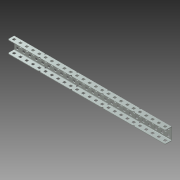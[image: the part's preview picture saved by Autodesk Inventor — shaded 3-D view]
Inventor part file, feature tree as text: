
AUTODESK INVENTOR PART (.ipt)
format: ipt  version: 2013 (Build 170138000, 138)  size: 2,703,360 bytes
history: native  units: mm (DEFAULTED — no unit token found)
features: other x124, extrude x124, pattern_linear x3, sketch x2, imported_body x1, plane x1, mirror x1
ambient origin geometry x8: Origin, YZ Plane, XZ Plane, XY Plane, X Axis, Y Axis, Z Axis, Center Point
bodies: Solid1 (feature_tree)
feature tree (256):
  imported_body  "Base1"
  sketch  "Sketch1"  dims[d1=1.1684mm]
  pattern_linear  "Rectangular Pattern1"  Spacing1=1.1684mm  [1 undecoded]
  pattern_linear  "Rectangular Pattern2"  Spacing1=0.0mm  [1 undecoded]
  pattern_linear  "Rectangular Pattern3"  Count1=25  [1 undecoded]
  plane  "Work Plane1"
  mirror  "Mirror1"
  other  "Srf1"
  other  "Srf2"
  other  "Srf3"
  other  "Srf4"
  other  "Srf5"
  other  "Srf6"
  other  "Srf7"
  other  "Srf8"
  other  "Srf9"
  other  "Srf10"
  other  "Srf11"
  other  "Srf12"
  other  "Srf13"
  other  "Srf14"
  other  "Srf15"
  other  "Srf16"
  other  "Srf17"
  other  "Srf18"
  other  "Srf19"
  other  "Srf20"
  other  "Srf21"
  other  "Srf22"
  other  "Srf23"
  other  "Srf24"
  other  "Srf25"
  other  "Srf26"
  other  "Srf27"
  other  "Srf28"
  other  "Srf29"
  other  "Srf30"
  other  "Srf31"
  other  "Srf32"
  other  "Srf33"
  other  "Srf34"
  other  "Srf35"
  other  "Srf36"
  other  "Srf37"
  other  "Srf38"
  other  "Srf39"
  other  "Srf40"
  other  "Srf41"
  other  "Srf42"
  other  "Srf43"
  other  "Srf44"
  other  "Srf45"
  other  "Srf46"
  other  "Srf47"
  other  "Srf48"
  other  "Srf49"
  other  "Srf50"
  other  "Srf51"
  other  "Srf52"
  other  "Srf53"
  other  "Srf54"
  other  "Srf55"
  other  "Srf56"
  other  "Srf57"
  other  "Srf58"
  other  "Srf59"
  other  "Srf60"
  other  "Srf61"
  other  "Srf62"
  other  "Srf63"
  other  "Srf64"
  other  "Srf65"
  other  "Srf66"
  other  "Srf67"
  other  "Srf68"
  other  "Srf69"
  other  "Srf70"
  other  "Srf71"
  other  "Srf72"
  other  "Srf73"
  other  "Srf74"
  sketch  "Sketch2"  dims[d2=0.0mm d3=1.1684mm d4=0.0mm d5=250.0mm d7=12.7mm d8=20.0mm d10=12.7mm d11=240.0mm d13=12.7mm d14=1.1684mm d15=0.0mm d16=250.0mm d18=12.7mm d19=0.0mm d20=0.0mm d21=0.0mm d22=0.0mm d23=0.0mm d24=0.0mm d25=0.0mm d26=0.0mm d27=0.0mm d28=0.0mm d29=0.0mm d30=0.0mm d31=0.0mm d32=0.0mm d33=0.0mm d34=0.0mm d35=0.0mm d36=0.0mm d37=0.0mm d38=0.0mm d39=0.0mm d40=0.0mm d41=0.0mm d42=0.0mm d43=0.0mm d44=0.0mm d45=0.0mm d46=0.0mm d47=0.0mm d48=0.0mm d49=0.0mm d50=0.0mm d51=0.0mm d52=0.0mm d53=0.0mm d54=0.0mm d55=0.0mm d56=0.0mm d57=0.0mm d58=0.0mm d59=0.0mm d60=0.0mm d61=0.0mm d62=0.0mm d63=0.0mm d64=0.0mm d65=0.0mm d66=0.0mm d67=0.0mm d68=0.0mm d69=0.0mm d70=0.0mm d71=0.0mm d72=0.0mm d73=0.0mm d74=0.0mm d75=0.0mm d76=0.0mm d77=0.0mm d78=0.0mm d79=0.0mm d80=0.0mm d81=0.0mm d82=0.0mm d83=0.0mm d84=0.0mm d85=0.0mm d86=0.0mm d87=0.0mm d88=0.0mm d89=0.0mm d90=0.0mm d91=0.0mm d92=0.0mm d93=0.0mm d94=0.0mm d95=0.0mm d96=0.0mm d97=0.0mm d98=0.0mm d99=0.0mm d100=0.0mm d101=0.0mm d102=0.0mm d103=0.0mm d104=0.0mm d105=0.0mm d106=0.0mm d107=0.0mm d108=0.0mm d109=0.0mm d110=0.0mm d111=0.0mm d112=0.0mm d113=0.0mm d114=0.0mm d115=0.0mm d116=0.0mm d117=0.0mm d118=0.0mm d119=0.0mm d120=0.0mm d121=0.0mm d122=0.0mm d123=0.0mm d124=0.0mm d125=0.0mm d126=0.0mm d127=0.0mm d128=0.0mm d129=0.0mm d130=0.0mm d131=0.0mm d132=0.0mm d133=0.0mm d134=0.0mm d135=0.0mm d136=0.0mm d137=0.0mm d138=0.0mm d139=0.0mm d140=0.0mm d141=0.0mm d142=0.0mm d143=0.0mm d144=0.0mm d145=0.0mm d146=0.0mm d147=0.0mm d148=0.0mm d149=0.0mm d150=0.0mm d151=0.0mm d152=0.0mm d153=0.0mm d154=0.0mm d155=0.0mm d156=0.0mm d157=0.0mm d158=0.0mm d159=0.0mm d160=0.0mm d161=0.0mm d162=0.0mm d163=0.0mm d164=0.0mm d165=0.0mm d166=0.0mm d167=0.0mm d168=0.0mm d169=0.0mm d170=0.0mm d171=0.0mm d172=0.0mm d173=0.0mm d174=0.0mm d175=0.0mm d176=0.0mm d177=0.0mm d178=0.0mm d179=0.0mm d180=0.0mm d181=0.0mm d182=0.0mm d183=0.0mm d184=0.0mm d185=0.0mm d186=0.0mm d187=0.0mm d188=0.0mm d189=0.0mm d190=0.0mm d191=0.0mm d192=0.0mm d193=0.0mm d194=0.0mm d195=0.0mm d196=0.0mm d197=0.0mm d198=0.0mm d199=0.0mm d200=0.0mm d201=0.0mm d202=0.0mm d203=0.0mm d204=0.0mm d205=0.0mm d206=0.0mm d207=0.0mm d208=0.0mm d209=0.0mm d210=0.0mm d211=0.0mm d212=0.0mm d213=0.0mm d214=0.0mm d215=0.0mm d216=0.0mm d217=0.0mm d218=0.0mm d219=0.0mm d220=0.0mm d221=0.0mm d222=0.0mm d223=0.0mm d224=0.0mm d225=0.0mm d226=0.0mm d227=0.0mm d228=0.0mm d229=0.0mm d230=0.0mm d231=0.0mm d232=0.0mm d233=0.0mm d234=0.0mm d235=0.0mm d236=0.0mm d237=0.0mm d238=0.0mm d239=0.0mm d240=0.0mm d241=0.0mm d242=0.0mm d243=0.0mm d244=0.0mm d245=0.0mm d246=0.0mm d247=0.0mm d248=0.0mm d249=0.0mm d250=0.0mm d251=0.0mm d252=0.0mm d253=0.0mm d254=0.0mm d255=0.0mm d256=0.0mm d257=0.0mm d258=0.0mm d259=0.0mm d260=0.0mm d261=0.0mm d262=0.0mm d263=0.0mm]
  other  "Srf75"
  other  "Srf76"
  other  "Srf77"
  other  "Srf78"
  other  "Srf79"
  other  "Srf80"
  other  "Srf81"
  other  "Srf82"
  other  "Srf83"
  other  "Srf84"
  other  "Srf85"
  other  "Srf86"
  other  "Srf87"
  other  "Srf88"
  other  "Srf89"
  other  "Srf90"
  other  "Srf91"
  other  "Srf92"
  other  "Srf93"
  other  "Srf94"
  other  "Srf95"
  other  "Srf96"
  other  "Srf97"
  other  "Srf98"
  other  "Srf99"
  other  "Srf100"
  other  "Srf101"
  other  "Srf102"
  other  "Srf103"
  other  "Srf104"
  other  "Srf105"
  other  "Srf106"
  other  "Srf107"
  other  "Srf108"
  other  "Srf109"
  other  "Srf110"
  other  "Srf111"
  other  "Srf112"
  other  "Srf113"
  other  "Srf114"
  other  "Srf115"
  other  "Srf116"
  other  "Srf117"
  other  "Srf118"
  other  "Srf119"
  other  "Srf120"
  other  "Srf121"
  other  "Srf122"
  other  "Srf123"
  other  "Srf124"
  extrude  "ExtrusionSrf1"  Depth=12.7mm
  extrude  "ExtrusionSrf2"  Depth=20.0mm
  extrude  "ExtrusionSrf75"  Depth=240.0mm
  extrude  "ExtrusionSrf3"  Depth=12.7mm
  extrude  "ExtrusionSrf4"  Depth=1.1684mm
  extrude  "ExtrusionSrf5"  TaperAngle=0.0deg  [1 undecoded]
  extrude  "ExtrusionSrf6"  Depth=250.0mm
  extrude  "ExtrusionSrf7"  Depth=12.7mm
  extrude  "ExtrusionSrf8"  TaperAngle=0.0deg  [1 undecoded]
  extrude  "ExtrusionSrf9"  TaperAngle=0.0deg  [1 undecoded]
  extrude  "ExtrusionSrf10"  TaperAngle=0.0deg  [1 undecoded]
  extrude  "ExtrusionSrf11"  TaperAngle=0.0deg  [1 undecoded]
  extrude  "ExtrusionSrf12"  TaperAngle=0.0deg  [1 undecoded]
  extrude  "ExtrusionSrf13"  TaperAngle=0.0deg  [1 undecoded]
  extrude  "ExtrusionSrf14"  TaperAngle=0.0deg  [1 undecoded]
  extrude  "ExtrusionSrf15"  TaperAngle=0.0deg  [1 undecoded]
  extrude  "ExtrusionSrf16"  TaperAngle=0.0deg  [1 undecoded]
  extrude  "ExtrusionSrf17"  TaperAngle=0.0deg  [1 undecoded]
  extrude  "ExtrusionSrf18"  TaperAngle=0.0deg  [1 undecoded]
  extrude  "ExtrusionSrf19"  TaperAngle=0.0deg  [1 undecoded]
  extrude  "ExtrusionSrf20"  TaperAngle=0.0deg  [1 undecoded]
  extrude  "ExtrusionSrf21"  TaperAngle=0.0deg  [1 undecoded]
  extrude  "ExtrusionSrf22"  TaperAngle=0.0deg  [1 undecoded]
  extrude  "ExtrusionSrf23"  TaperAngle=0.0deg  [1 undecoded]
  extrude  "ExtrusionSrf24"  TaperAngle=0.0deg  [1 undecoded]
  extrude  "ExtrusionSrf25"  TaperAngle=0.0deg  [1 undecoded]
  extrude  "ExtrusionSrf26"  TaperAngle=0.0deg  [1 undecoded]
  extrude  "ExtrusionSrf27"  TaperAngle=0.0deg  [1 undecoded]
  extrude  "ExtrusionSrf28"  TaperAngle=0.0deg  [1 undecoded]
  extrude  "ExtrusionSrf29"  TaperAngle=0.0deg  [1 undecoded]
  extrude  "ExtrusionSrf30"  TaperAngle=0.0deg  [1 undecoded]
  extrude  "ExtrusionSrf31"  TaperAngle=0.0deg  [1 undecoded]
  extrude  "ExtrusionSrf32"  TaperAngle=0.0deg  [1 undecoded]
  extrude  "ExtrusionSrf33"  TaperAngle=0.0deg  [1 undecoded]
  extrude  "ExtrusionSrf34"  TaperAngle=0.0deg  [1 undecoded]
  extrude  "ExtrusionSrf35"  TaperAngle=0.0deg  [1 undecoded]
  extrude  "ExtrusionSrf36"  TaperAngle=0.0deg  [1 undecoded]
  extrude  "ExtrusionSrf37"  TaperAngle=0.0deg  [1 undecoded]
  extrude  "ExtrusionSrf38"  TaperAngle=0.0deg  [1 undecoded]
  extrude  "ExtrusionSrf39"  TaperAngle=0.0deg  [1 undecoded]
  extrude  "ExtrusionSrf40"  TaperAngle=0.0deg  [1 undecoded]
  extrude  "ExtrusionSrf41"  TaperAngle=0.0deg  [1 undecoded]
  extrude  "ExtrusionSrf42"  TaperAngle=0.0deg  [1 undecoded]
  extrude  "ExtrusionSrf43"  TaperAngle=0.0deg  [1 undecoded]
  extrude  "ExtrusionSrf44"  TaperAngle=0.0deg  [1 undecoded]
  extrude  "ExtrusionSrf45"  TaperAngle=0.0deg  [1 undecoded]
  extrude  "ExtrusionSrf46"  TaperAngle=0.0deg  [1 undecoded]
  extrude  "ExtrusionSrf47"  TaperAngle=0.0deg  [1 undecoded]
  extrude  "ExtrusionSrf48"  TaperAngle=0.0deg  [1 undecoded]
  extrude  "ExtrusionSrf49"  TaperAngle=0.0deg  [1 undecoded]
  extrude  "ExtrusionSrf50"  TaperAngle=0.0deg  [1 undecoded]
  extrude  "ExtrusionSrf51"  TaperAngle=0.0deg  [1 undecoded]
  extrude  "ExtrusionSrf52"  TaperAngle=0.0deg  [1 undecoded]
  extrude  "ExtrusionSrf53"  TaperAngle=0.0deg  [1 undecoded]
  extrude  "ExtrusionSrf54"  TaperAngle=0.0deg  [1 undecoded]
  extrude  "ExtrusionSrf55"  TaperAngle=0.0deg  [1 undecoded]
  extrude  "ExtrusionSrf56"  TaperAngle=0.0deg  [1 undecoded]
  extrude  "ExtrusionSrf57"  TaperAngle=0.0deg  [1 undecoded]
  extrude  "ExtrusionSrf58"  TaperAngle=0.0deg  [1 undecoded]
  extrude  "ExtrusionSrf59"  TaperAngle=0.0deg  [1 undecoded]
  extrude  "ExtrusionSrf60"  TaperAngle=0.0deg  [1 undecoded]
  extrude  "ExtrusionSrf61"  TaperAngle=0.0deg  [1 undecoded]
  extrude  "ExtrusionSrf62"  TaperAngle=0.0deg  [1 undecoded]
  extrude  "ExtrusionSrf63"  TaperAngle=0.0deg  [1 undecoded]
  extrude  "ExtrusionSrf64"  TaperAngle=0.0deg  [1 undecoded]
  extrude  "ExtrusionSrf65"  TaperAngle=0.0deg  [1 undecoded]
  extrude  "ExtrusionSrf66"  TaperAngle=0.0deg  [1 undecoded]
  extrude  "ExtrusionSrf67"  TaperAngle=0.0deg  [1 undecoded]
  extrude  "ExtrusionSrf68"  TaperAngle=0.0deg  [1 undecoded]
  extrude  "ExtrusionSrf69"  TaperAngle=0.0deg  [1 undecoded]
  extrude  "ExtrusionSrf70"  TaperAngle=0.0deg  [1 undecoded]
  extrude  "ExtrusionSrf71"  TaperAngle=0.0deg  [1 undecoded]
  extrude  "ExtrusionSrf72"  TaperAngle=0.0deg  [1 undecoded]
  extrude  "ExtrusionSrf73"  TaperAngle=0.0deg  [1 undecoded]
  extrude  "ExtrusionSrf74"  TaperAngle=0.0deg  [1 undecoded]
  extrude  "ExtrusionSrf76"  TaperAngle=0.0deg  [1 undecoded]
  extrude  "ExtrusionSrf77"  TaperAngle=0.0deg  [1 undecoded]
  extrude  "ExtrusionSrf78"  TaperAngle=0.0deg  [1 undecoded]
  extrude  "ExtrusionSrf79"  TaperAngle=0.0deg  [1 undecoded]
  extrude  "ExtrusionSrf80"  TaperAngle=0.0deg  [1 undecoded]
  extrude  "ExtrusionSrf81"  TaperAngle=0.0deg  [1 undecoded]
  extrude  "ExtrusionSrf82"  TaperAngle=0.0deg  [1 undecoded]
  extrude  "ExtrusionSrf83"  TaperAngle=0.0deg  [1 undecoded]
  extrude  "ExtrusionSrf84"  TaperAngle=0.0deg  [1 undecoded]
  extrude  "ExtrusionSrf85"  TaperAngle=0.0deg  [1 undecoded]
  extrude  "ExtrusionSrf86"  TaperAngle=0.0deg  [1 undecoded]
  extrude  "ExtrusionSrf87"  TaperAngle=0.0deg  [1 undecoded]
  extrude  "ExtrusionSrf88"  TaperAngle=0.0deg  [1 undecoded]
  extrude  "ExtrusionSrf89"  TaperAngle=0.0deg  [1 undecoded]
  extrude  "ExtrusionSrf90"  TaperAngle=0.0deg  [1 undecoded]
  extrude  "ExtrusionSrf91"  TaperAngle=0.0deg  [1 undecoded]
  extrude  "ExtrusionSrf92"  TaperAngle=0.0deg  [1 undecoded]
  extrude  "ExtrusionSrf93"  TaperAngle=0.0deg  [1 undecoded]
  extrude  "ExtrusionSrf94"  TaperAngle=0.0deg  [1 undecoded]
  extrude  "ExtrusionSrf95"  TaperAngle=0.0deg  [1 undecoded]
  extrude  "ExtrusionSrf96"  TaperAngle=0.0deg  [1 undecoded]
  extrude  "ExtrusionSrf97"  TaperAngle=0.0deg  [1 undecoded]
  extrude  "ExtrusionSrf98"  TaperAngle=0.0deg  [1 undecoded]
  extrude  "ExtrusionSrf99"  TaperAngle=0.0deg  [1 undecoded]
  extrude  "ExtrusionSrf100"  TaperAngle=0.0deg  [1 undecoded]
  extrude  "ExtrusionSrf101"  TaperAngle=0.0deg  [1 undecoded]
  extrude  "ExtrusionSrf102"  TaperAngle=0.0deg  [1 undecoded]
  extrude  "ExtrusionSrf103"  TaperAngle=0.0deg  [1 undecoded]
  extrude  "ExtrusionSrf104"  TaperAngle=0.0deg  [1 undecoded]
  extrude  "ExtrusionSrf105"  TaperAngle=0.0deg  [1 undecoded]
  extrude  "ExtrusionSrf106"  TaperAngle=0.0deg  [1 undecoded]
  extrude  "ExtrusionSrf107"  TaperAngle=0.0deg  [1 undecoded]
  extrude  "ExtrusionSrf108"  TaperAngle=0.0deg  [1 undecoded]
  extrude  "ExtrusionSrf109"  TaperAngle=0.0deg  [1 undecoded]
  extrude  "ExtrusionSrf110"  TaperAngle=0.0deg  [1 undecoded]
  extrude  "ExtrusionSrf111"  TaperAngle=0.0deg  [1 undecoded]
  extrude  "ExtrusionSrf112"  TaperAngle=0.0deg  [1 undecoded]
  extrude  "ExtrusionSrf113"  TaperAngle=0.0deg  [1 undecoded]
  extrude  "ExtrusionSrf114"  TaperAngle=0.0deg  [1 undecoded]
  extrude  "ExtrusionSrf115"  TaperAngle=0.0deg  [1 undecoded]
  extrude  "ExtrusionSrf116"  TaperAngle=0.0deg  [1 undecoded]
  extrude  "ExtrusionSrf117"  TaperAngle=0.0deg  [1 undecoded]
  extrude  "ExtrusionSrf118"  TaperAngle=0.0deg  [1 undecoded]
  extrude  "ExtrusionSrf119"  TaperAngle=0.0deg  [1 undecoded]
  extrude  "ExtrusionSrf120"  TaperAngle=0.0deg  [1 undecoded]
  extrude  "ExtrusionSrf121"  TaperAngle=0.0deg  [1 undecoded]
  extrude  "ExtrusionSrf122"  TaperAngle=0.0deg  [1 undecoded]
  extrude  "ExtrusionSrf123"  TaperAngle=0.0deg  [1 undecoded]
  extrude  "ExtrusionSrf124"  TaperAngle=0.0deg  [1 undecoded]
note: 120 required parameter values undecoded (feature->parameter linkage not recoverable at this tier; creation-order binding heuristic only, values carry confidence <= 0.55)
